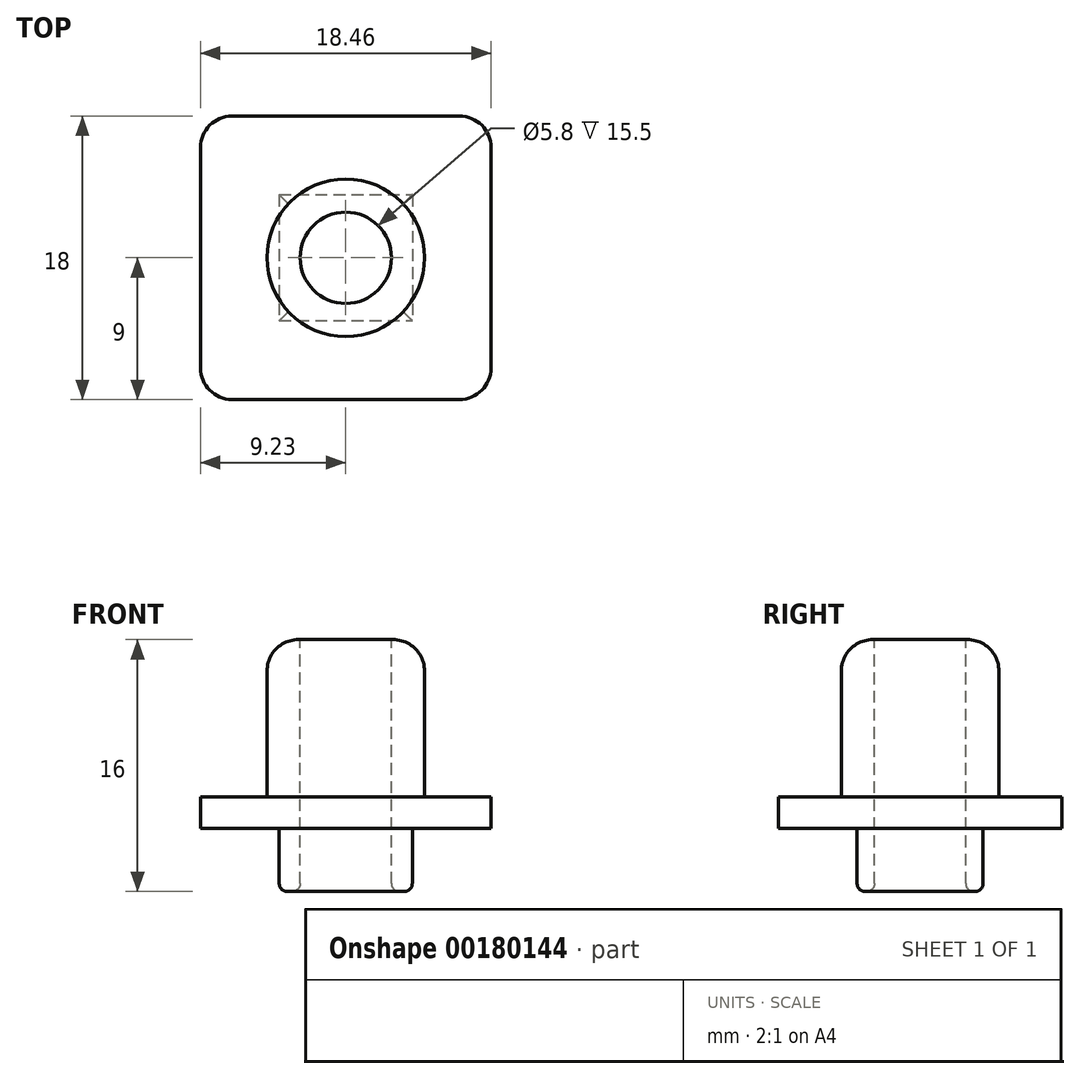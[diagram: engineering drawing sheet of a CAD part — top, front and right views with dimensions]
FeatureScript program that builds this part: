
annotation { "Feature Type Name" : "Feature", "Feature Type Description" : "" }
export const myFeature = defineFeature(function(context is Context, id is Id, definition is map)
    precondition{}
    {
        {
            var Q0;
            Q0=qCreatedBy(makeId("Top.planeOp"),FACE);
            var sketch = newSketch(context, id + "F0", { "sketchPlane" : qUnion([Q0])});
            skLineSegment(sketch, "E0.bottom", {"start": v(-4.22, 4) * mm, "end": v(4.22, 4) * mm});
            skLineSegment(sketch, "E0.top", {"start": v(-4.22, -4) * mm, "end": v(4.22, -4) * mm});
            skLineSegment(sketch, "E0.left", {"start": v(-4.22, 4) * mm, "end": v(-4.22, -4) * mm});
            skLineSegment(sketch, "E0.right", {"start": v(4.22, 4) * mm, "end": v(4.22, -4) * mm});
            skSolve(sketch);
        }
        {
            var Q0;
            Q0 = qSketchRegion(id + "F0", true);
            extrude(context, id + "F1", {"entities" : qUnion([Q0]), "depth" : 4 * mm});
        }
        {
            var Q0;
            Q0=makeQuery(id+"F1.opExtrude","CAP_FACE",FACE,{"disambiguationData":[OSD([sQuery(id+"F0.wireOp",EDGE,"E0.bottom"),sQuery(id+"F0.wireOp",EDGE,"E0.top"),sQuery(id+"F0.wireOp",EDGE,"E0.left"),sQuery(id+"F0.wireOp",EDGE,"E0.right")])],"isStart":false});
            var sketch = newSketch(context, id + "F2", { "sketchPlane" : qUnion([Q0])});
            skLineSegment(sketch, "E1.0", {"start": v(-9.22, 9) * mm, "end": v(9.22, 9) * mm});
            skLineSegment(sketch, "E1.1", {"start": v(-9.22, 9) * mm, "end": v(-9.22, -9) * mm});
            skLineSegment(sketch, "E1.2", {"start": v(-9.22, -9) * mm, "end": v(9.22, -9) * mm});
            skLineSegment(sketch, "E1.3", {"start": v(9.22, 9) * mm, "end": v(9.22, -9) * mm});
            skSolve(sketch);
        }
        {
            var Q0;
            Q0 = qSketchRegion(id + "F2", true);
            extrude(context, id + "F3", {"entities" : qUnion([Q0]), "operationType" : NewBodyOperationType.ADD, "depth" : 2 * mm});
        }
        {
            var Q0;
            Q0=makeQuery(id+"F3.opExtrude","CAP_FACE",FACE,{"disambiguationData":[OSD([sQuery(id+"F2.wireOp",EDGE,"E1.0"),sQuery(id+"F2.wireOp",EDGE,"E1.1"),sQuery(id+"F2.wireOp",EDGE,"E1.2"),sQuery(id+"F2.wireOp",EDGE,"E1.3")])],"isStart":false});
            var sketch = newSketch(context, id + "F4", { "sketchPlane" : qUnion([Q0])});
            skCircle(sketch, "E2", {"center": v(0, 0) * mm, "radius": 5 * mm});
            skSolve(sketch);
        }
        {
            var Q0;
            Q0 = qSketchRegion(id + "F4", true);
            extrude(context, id + "F5", {"entities" : qUnion([Q0]), "operationType" : NewBodyOperationType.ADD, "depth" : 10 * mm});
        }
        {
            var Q0;
            Q0=makeQuery(id+"F5.opExtrude","CAP_FACE",FACE,{"disambiguationData":[OSD([sQuery(id+"F4.wireOp",EDGE,"E2")])],"isStart":false});
            var sketch = newSketch(context, id + "F6", { "sketchPlane" : qUnion([Q0])});
            skCircle(sketch, "E3", {"center": v(0, 0) * mm, "radius": 2.9 * mm});
            skSolve(sketch);
        }
        {
            var Q0;
            Q0 = qSketchRegion(id + "F6", true);
            extrude(context, id + "F7", {"entities" : qUnion([Q0]), "operationType" : NewBodyOperationType.REMOVE, "endBound" : BoundingType.THROUGH_ALL, "oppositeDirection" : true, "depth" : 25 * mm});
        }
        {
            var Q0;
            Q0=makeQuery(id+"F3.opExtrude","SWEPT_EDGE",EDGE,{"disambiguationData":[OSD([sQuery(id+"F2.wireOp",EDGE,"E1.0"),sQuery(id+"F2.wireOp",EDGE,"E1.1")])]});
            var Q1;
            Q1=makeQuery(id+"F3.opExtrude","SWEPT_EDGE",EDGE,{"disambiguationData":[OSD([sQuery(id+"F2.wireOp",EDGE,"E1.0"),sQuery(id+"F2.wireOp",EDGE,"E1.3")])]});
            var Q2;
            Q2=makeQuery(id+"F3.opExtrude","SWEPT_EDGE",EDGE,{"disambiguationData":[OSD([sQuery(id+"F2.wireOp",EDGE,"E1.2"),sQuery(id+"F2.wireOp",EDGE,"E1.3")])]});
            var Q3;
            Q3=makeQuery(id+"F3.opExtrude","SWEPT_EDGE",EDGE,{"disambiguationData":[OSD([sQuery(id+"F2.wireOp",EDGE,"E1.1"),sQuery(id+"F2.wireOp",EDGE,"E1.2")])]});
            var Q4;
            Q4=makeQuery(id+"F5.opExtrude","CAP_EDGE",EDGE,{"disambiguationData":[OSD([sQuery(id+"F4.wireOp",EDGE,"E2")])],"isStart":false});
            fillet(context, id + "F8", {"entities" : qUnion([Q0, Q1, Q2, Q3, Q4]), "radius" : 2 * mm, "tangentPropagation" : true, "allowEdgeOverflow" : false});
        }
        {
            var Q0;
            Q0=makeQuery(id+"F7.boolean.opBoolean","COPY",EDGE,{"derivedFrom":makeQuery(id+"F7.opExtrude","CAP_EDGE",EDGE,{"disambiguationData":[OSD([sQuery(id+"F6.wireOp",EDGE,"E3")])],"isStart":true})});
            var Q1;
            Q1=makeQuery(id+"F7.boolean.opBoolean","INTERSECT",EDGE,{"derivedFrom":[makeQuery(id+"F1.opExtrude","CAP_FACE",FACE,{"disambiguationData":[OSD([sQuery(id+"F0.wireOp",EDGE,"E0.bottom"),sQuery(id+"F0.wireOp",EDGE,"E0.top"),sQuery(id+"F0.wireOp",EDGE,"E0.left"),sQuery(id+"F0.wireOp",EDGE,"E0.right")])],"isStart":true}),makeQuery(id+"F7.opExtrude","SWEPT_FACE",FACE,{"disambiguationData":[OSD([sQuery(id+"F6.wireOp",EDGE,"E3")])]})]});
            var Q2;
            Q2=makeQuery(id+"F1.opExtrude","CAP_EDGE",EDGE,{"disambiguationData":[OSD([sQuery(id+"F0.wireOp",EDGE,"E0.left")])],"isStart":true});
            var Q3;
            Q3=makeQuery(id+"F1.opExtrude","CAP_EDGE",EDGE,{"disambiguationData":[OSD([sQuery(id+"F0.wireOp",EDGE,"E0.bottom")])],"isStart":true});
            var Q4;
            Q4=makeQuery(id+"F1.opExtrude","CAP_EDGE",EDGE,{"disambiguationData":[OSD([sQuery(id+"F0.wireOp",EDGE,"E0.top")])],"isStart":true});
            var Q5;
            Q5=makeQuery(id+"F1.opExtrude","CAP_EDGE",EDGE,{"disambiguationData":[OSD([sQuery(id+"F0.wireOp",EDGE,"E0.right")])],"isStart":true});
            fillet(context, id + "F9", {"entities" : qUnion([Q0, Q1, Q2, Q3, Q4, Q5]), "radius" : 0.5 * mm, "tangentPropagation" : true, "allowEdgeOverflow" : false});
        }
    });
